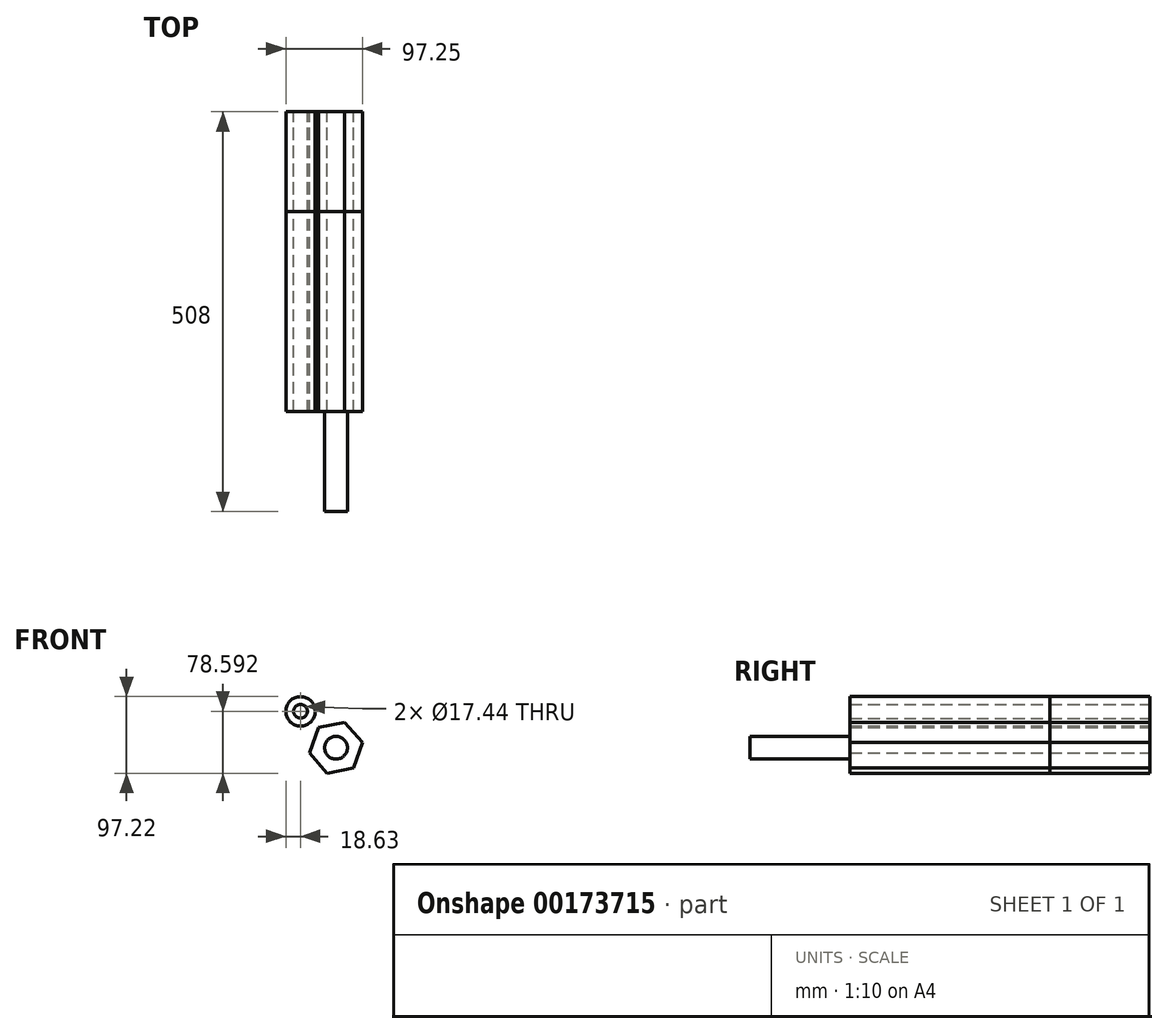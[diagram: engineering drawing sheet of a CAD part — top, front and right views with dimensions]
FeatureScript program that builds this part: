
annotation { "Feature Type Name" : "Feature", "Feature Type Description" : "" }
export const myFeature = defineFeature(function(context is Context, id is Id, definition is map)
    precondition{}
    {
        {
            var Q0;
            Q0=qCreatedBy(makeId("Front.planeOp"),FACE);
            var sketch = newSketch(context, id + "F0", { "sketchPlane" : qUnion([Q0])});
            skCircle(sketch, "E0.cCircle", {"center": v(0, 0) * mm, "radius": 29.58 * mm, "construction": true});
            skLineSegment(sketch, "E0.0", {"start": v(-22.43, 25.76) * mm, "end": v(11.1, 32.3) * mm});
            skLineSegment(sketch, "E0.1", {"start": v(11.1, 32.3) * mm, "end": v(33.52, 6.55) * mm});
            skLineSegment(sketch, "E0.2", {"start": v(33.52, 6.55) * mm, "end": v(22.43, -25.76) * mm});
            skLineSegment(sketch, "E0.3", {"start": v(22.43, -25.76) * mm, "end": v(-11.1, -32.3) * mm});
            skLineSegment(sketch, "E0.4", {"start": v(-11.1, -32.3) * mm, "end": v(-33.52, -6.55) * mm});
            skLineSegment(sketch, "E0.5", {"start": v(-33.52, -6.55) * mm, "end": v(-22.43, 25.76) * mm});
            skPoint(sketch, "E0.0.midPoint", {"position": v(-5.67, 29.03) * mm});
            skCircle(sketch, "E1", {"center": v(-45.1, 46.28) * mm, "radius": 18.63 * mm});
            skCircle(sketch, "E2", {"center": v(-45.1, 46.28) * mm, "radius": 8.72 * mm});
            skSolve(sketch);
        }
        {
            var Q0;
            Q0 = qSketchRegion(id + "F0", true);
            extrude(context, id + "F1", {"entities" : qUnion([Q0]), "depth" : 254 * mm});
        }
        {
            var Q0;
            Q0=makeQuery(id+"F1.opExtrude","CAP_FACE",FACE,{"disambiguationData":[OSD([sQuery(id+"F0.wireOp",EDGE,"E1")])],"isStart":false});
            var sketch = newSketch(context, id + "F2", { "sketchPlane" : qUnion([Q0])});
            skCircle(sketch, "E3", {"center": v(0, 0) * mm, "radius": 17.11 * mm});
            skSolve(sketch);
        }
        {
            var Q0;
            Q0=makeQuery(id+"F2.imprint","IMPRINT",FACE,{"disambiguationData":[TD([[makeQuery(id+"F2.imprint","IMPRINT",EDGE,{"derivedFrom":sQuery(id+"F2.wireOp",EDGE,"E3")}),1.0]])]});
            var Q1;
            Q1=makeQuery(id+"F1.opExtrude","CAP_FACE",FACE,{"disambiguationData":[OSD([sQuery(id+"F0.wireOp",EDGE,"E0.0"),sQuery(id+"F0.wireOp",EDGE,"E0.1"),sQuery(id+"F0.wireOp",EDGE,"E0.2"),sQuery(id+"F0.wireOp",EDGE,"E0.3"),sQuery(id+"F0.wireOp",EDGE,"E0.4"),sQuery(id+"F0.wireOp",EDGE,"E0.5")])],"isStart":false});
            var Q2;
            Q2=makeQuery(id+"F2.imprint","IMPRINT",FACE,{"disambiguationData":[TD([[makeQuery(id+"F2.imprint","IMPRINT",EDGE,{"derivedFrom":makeQuery(id+"F1.opExtrude","CAP_EDGE",EDGE,{"disambiguationData":[OSD([sQuery(id+"F0.wireOp",EDGE,"E1")])],"isStart":false})}),1.0]])]});
            extrude(context, id + "F3", {"entities" : qUnion([Q0, Q1, Q2]), "operationType" : NewBodyOperationType.ADD, "depth" : 127 * mm});
        }
        {
            var Q0;
            Q0 = qSketchRegion(id + "F0", true);
            extrude(context, id + "F4", {"entities" : qUnion([Q0]), "depth" : 127 * mm});
        }
        {
            var Q0;
            Q0=makeQuery(id+"F3.opExtrude","CAP_FACE",FACE,{"disambiguationData":[OSD([sQuery(id+"F0.wireOp",EDGE,"E0.0"),sQuery(id+"F0.wireOp",EDGE,"E0.1"),sQuery(id+"F0.wireOp",EDGE,"E0.2"),sQuery(id+"F0.wireOp",EDGE,"E0.3"),sQuery(id+"F0.wireOp",EDGE,"E0.4"),sQuery(id+"F0.wireOp",EDGE,"E0.5")])],"isStart":false});
            var sketch = newSketch(context, id + "F5", { "sketchPlane" : qUnion([Q0])});
            skSolve(sketch);
        }
        {
            var Q0;
            Q0=makeQuery(id+"F5.imprint","IMPRINT",FACE,{"disambiguationData":[TD([[makeQuery(id+"F5.imprint","IMPRINT",EDGE,{"derivedFrom":makeQuery(id+"F3.opExtrude","CAP_EDGE",EDGE,{"disambiguationData":[OSD([sQuery(id+"F0.wireOp",EDGE,"E0.0")])],"isStart":false})}),-1.0]])]});
            var sketch = newSketch(context, id + "F6", { "sketchPlane" : qUnion([Q0])});
            skCircle(sketch, "E4", {"center": v(0, 0) * mm, "radius": 14.45 * mm});
            skSolve(sketch);
        }
        {
            var Q0;
            Q0 = qSketchRegion(id + "F6", true);
            var Q1;
            Q1=makeQuery(id+"F1.opExtrude","CAP_FACE",FACE,{"disambiguationData":[OSD([sQuery(id+"F0.wireOp",EDGE,"E0.0"),sQuery(id+"F0.wireOp",EDGE,"E0.1"),sQuery(id+"F0.wireOp",EDGE,"E0.2"),sQuery(id+"F0.wireOp",EDGE,"E0.3"),sQuery(id+"F0.wireOp",EDGE,"E0.4"),sQuery(id+"F0.wireOp",EDGE,"E0.5")])],"isStart":true});
            extrude(context, id + "F7", {"entities" : qUnion([Q0, Q1]), "depth" : 127 * mm});
        }
    });
